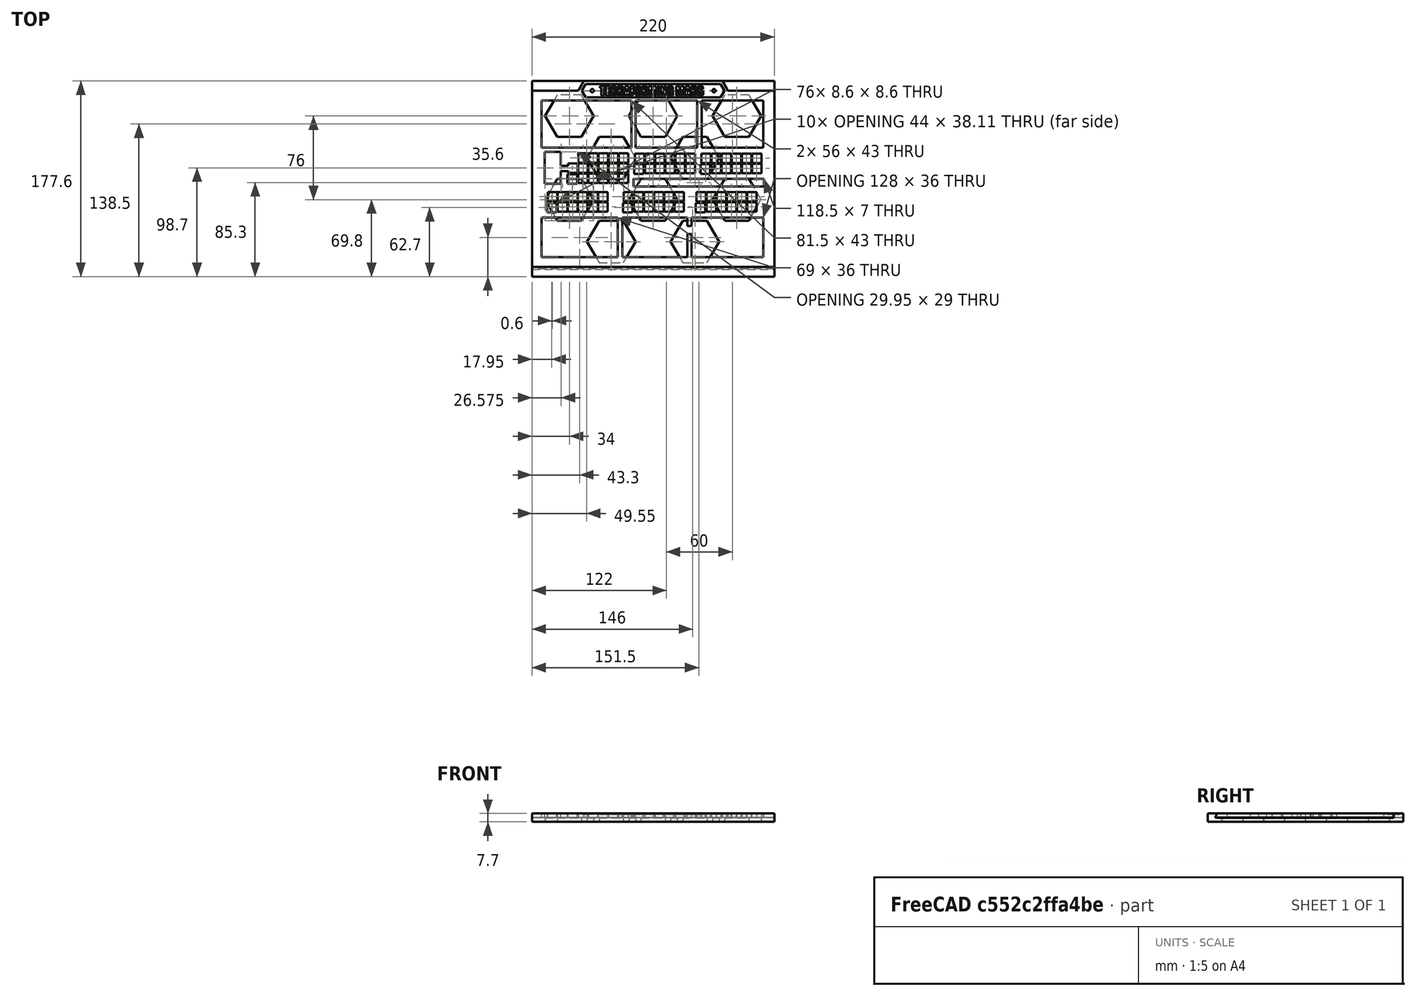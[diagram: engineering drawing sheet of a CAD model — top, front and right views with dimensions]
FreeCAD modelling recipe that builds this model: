
FCSTD DOCUMENT  (FreeCAD 0.21R33668 +26 (Git))
Label: overlay-full-v5
License: All rights reserved
LicenseURL: https://en.wikipedia.org/wiki/All_rights_reserved
objects: Sketcher::SketchObject×11, PartDesign::Pad×9, PartDesign::Pocket×5, Part::Feature×2, Part::Part2DObjectPython×2, PartDesign::Body×2, Mesh::Feature×1, Part::Refine×1, PartDesign::FeatureBase×1, Part::Extrusion×1
note: 48 computed .brp shape members not serialized (recipe doc carries the construction recipe); baked Part::Feature solids carry a one-line shape summary decoded from their .brp

FEATURE [Mesh::Feature] Terraforming_Mars_overlay
FEATURE [Part::Feature] Terraforming_Mars_overlay001
  shape: bbox 208 x 148 x 3.7 mm, 1736 faces, 0 solids (baked)
FEATURE [Part::Feature] Terraforming_Mars_overlay001_solid  label="Terraforming_Mars_overlay001 (Solid)"
  shape: bbox 208 x 148 x 3.7 mm, 1736 faces (baked)
FEATURE [Part::Refine] Terraforming_Mars_overlay001_solid001  label="Terraforming_Mars_overlay001 (Solid)001"
  Source = -> Terraforming_Mars_overlay001_solid
FEATURE [PartDesign::FeatureBase] BaseFeature
  BaseFeature = -> Terraforming_Mars_overlay001_solid001
FEATURE [Sketcher::SketchObject] Sketch
  ExternalGeometry = -> [BaseFeature]
  FullyConstrained = true
  MapMode = 5
  Placement = pos=(0,0,3.7) rot=(0,0,1;0rad)
  Support = -> [BaseFeature]
  sketch-geometry (8):
    g0: LineSegment StartX=6 StartY=154 StartZ=0 EndX=214 EndY=154 EndZ=0
    g1: LineSegment StartX=214 StartY=154 StartZ=0 EndX=214 EndY=6 EndZ=0
    g2: LineSegment StartX=214 StartY=6 StartZ=0 EndX=6 EndY=6 EndZ=0
    g3: LineSegment StartX=6 StartY=6 StartZ=0 EndX=6 EndY=154 EndZ=0
    g4: LineSegment StartX=0 StartY=160 StartZ=0 EndX=220 EndY=160 EndZ=0
    g5: LineSegment StartX=220 StartY=160 StartZ=0 EndX=220 EndY=0 EndZ=0
    g6: LineSegment StartX=220 StartY=0 StartZ=0 EndX=0 EndY=0 EndZ=0
    g7: LineSegment StartX=0 StartY=0 StartZ=0 EndX=0 EndY=160 EndZ=0
  constraints (22):
    c: Coincident(g0,g1)
    c: Coincident(g1,g2)
    c: Coincident(g2,g3)
    c: Coincident(g3,g0)
    c: Horizontal(g0)
    c: Horizontal(g2)
    c: Vertical(g1)
    c: Vertical(g3)
    c: Coincident(g0,g-3)
    c: Coincident(g1,g-4)
    c: Coincident(g4,g5)
    c: Coincident(g5,g6)
    c: Coincident(g6,g7)
    c: Coincident(g7,g4)
    c: Horizontal(g4)
    c: Horizontal(g6)
    c: Vertical(g5)
    c: Vertical(g7)
    c: DistanceX(g4,g0) = 6
    c: DistanceX(g0,g4) = 6
    c: DistanceY(g0,g4) = 6
    c: DistanceY(g5,g1) = 6
FEATURE [PartDesign::Pad] Pad
  BaseFeature = -> BaseFeature
  Direction = (0,0,1)
  Length = 10
  Length2 = 10
  Profile = -> Sketch
  ReferenceAxis = -> Sketch [N_Axis]
  Type = 3
  UpToFace = -> BaseFeature [Face1]
FEATURE [Sketcher::SketchObject] Sketch001
  ExternalGeometry = -> [Pad]
  FullyConstrained = true
  MapMode = 5
  Placement = pos=(0,0,3.7) rot=(0,0,1;0rad)
  Support = -> [Pad]
  sketch-geometry (5):
    g0: GeomPoint X=110 Y=160 Z=0
    g1: LineSegment StartX=42 StartY=160 StartZ=0 EndX=47.0807 EndY=168.8 EndZ=0
    g2: LineSegment StartX=47.0807 StartY=168.8 StartZ=0 EndX=172.919 EndY=168.8 EndZ=0
    g3: LineSegment StartX=172.919 StartY=168.8 StartZ=0 EndX=178 EndY=160 EndZ=0
    g4: LineSegment StartX=178 StartY=160 StartZ=0 EndX=42 EndY=160 EndZ=0
  constraints (13):
    c: Symmetric(g-3,g-3,g0)
    c: Coincident(g1,g2)
    c: Horizontal(g2)
    c: Coincident(g2,g3)
    c: Coincident(g3,g4)
    c: Coincident(g4,g1)
    c: Angle(g1,g4,g1) = 2.0944
    c: Angle(g4,g3,g3) = 2.0944
    c: DistanceY(g1,g1) = 8.8
    c: PointOnObject(g1,g-3)
    c: DistanceX(g-3,g1) = 42
    c: DistanceX(g3,g-3) = 42
    c: PointOnObject(g3,g-3)
FEATURE [PartDesign::Pad] Pad001
  BaseFeature = -> Pad
  Direction = (0,0,1)
  Length = 10
  Length2 = 10
  Profile = -> Sketch001
  ReferenceAxis = -> Sketch001 [N_Axis]
  Type = 3
  UpToFace = -> Pad [Face2]
FEATURE [Sketcher::SketchObject] Sketch002
  ExternalGeometry = -> [Pad001]
  FullyConstrained = true
  MapMode = 5
  Placement = pos=(0,0,3.7) rot=(0,0,1;0rad)
  Support = -> [Pad001]
  sketch-geometry (7):
    g0: GeomPoint X=110 Y=160 Z=0
    g1: LineSegment StartX=45.2332 StartY=160 StartZ=0 EndX=48.6973 EndY=166 EndZ=0
    g2: LineSegment StartX=48.6973 StartY=166 StartZ=0 EndX=171.303 EndY=166 EndZ=0
    g3: LineSegment StartX=171.303 StartY=166 StartZ=0 EndX=174.767 EndY=160 EndZ=0
    g4: LineSegment StartX=174.767 StartY=160 StartZ=0 EndX=171.303 EndY=154 EndZ=0
    g5: LineSegment StartX=171.303 StartY=154 StartZ=0 EndX=48.6973 EndY=154 EndZ=0
    g6: LineSegment StartX=48.6973 StartY=154 StartZ=0 EndX=45.2332 EndY=160 EndZ=0
  constraints (17):
    c: Symmetric(g-4,g-4,g0)
    c: PointOnObject(g1,g-4)
    c: Coincident(g1,g2)
    c: Horizontal(g2)
    c: Coincident(g2,g3)
    c: PointOnObject(g3,g-4)
    c: Coincident(g3,g4)
    c: PointOnObject(g4,g-5)
    c: Coincident(g4,g5)
    c: Coincident(g5,g6)
    c: Coincident(g6,g1)
    c: Parallel(g1,g-6)
    c: Symmetric(g5,g1,g-4)
    c: Symmetric(g4,g2,g-4)
    c: Parallel(g3,g-7)
    c: Distance(g1,g-6) = 2.8
    c: Distance(g2,g-7) = 2.8
FEATURE [PartDesign::Pocket] Pocket
  BaseFeature = -> Pad001
  Direction = (0,0,-1)
  Length = 1
  Length2 = 5
  Profile = -> Sketch002
  ReferenceAxis = -> Sketch002 [N_Axis]
  Type = 0
FEATURE [Part::Part2DObjectPython] ShapeString  # Draft 2D object (typed FeaturePython)
  FontFile = <path>
  MakeFace = true
  Placement = pos=(61.7,155.5,2.7) rot=(0,0,1;0rad)
  Size = 9
  String = TERRAFORMING MARS
  Tracking = 0
FEATURE [Sketcher::SketchObject] Sketch003
  ExternalGeometry = -> [Pocket]
  FullyConstrained = true
  MapMode = 5
  Placement = pos=(0,0,2.7) rot=(0,0,1;0rad)
  Support = -> [Pocket]
  sketch-geometry (3):
    g0: LineSegment StartX=45.2332 StartY=160 StartZ=0 EndX=174.767 EndY=160 EndZ=0
    g1: Circle CenterX=54.7332 CenterY=160 CenterZ=0 NormalX=0 NormalY=0 NormalZ=1 AngleXU=0 Radius=1.5
    g2: Circle CenterX=165.267 CenterY=160 CenterZ=0 NormalX=0 NormalY=0 NormalZ=1 AngleXU=0 Radius=1.5
  constraints (8):
    c: Coincident(g0,g-3)
    c: Coincident(g0,g-4)
    c: PointOnObject(g1,g0)
    c: PointOnObject(g2,g0)
    c: Diameter(g2) = 3
    c: Diameter(g1) = 3
    c: DistanceX(g0,g1) = 9.5
    c: DistanceX(g2,g0) = 9.5
FEATURE [PartDesign::Pad] Pad002
  BaseFeature = -> Pocket
  Direction = (0,0,1)
  Length = 1
  Length2 = 10
  Profile = -> Sketch003
  ReferenceAxis = -> Sketch003 [N_Axis]
  Type = 0
FEATURE [PartDesign::Pad] Pad003
  BaseFeature = -> Pad002
  Direction = (0,-1,0)
  Length = 2
  Length2 = 10
  Profile = -> Pad002 [Face352]
  Type = 0
FEATURE [Sketcher::SketchObject] Sketch004
  ExternalGeometry = -> [Pad003]
  FullyConstrained = true
  MapMode = 5
  Placement = pos=(220,0,0) rot=(0.57735,0.57735,0.57735;2.0944rad)
  Support = -> [Pad003]
  sketch-geometry (3):
    g0: LineSegment StartX=0 StartY=3.7 StartZ=0 EndX=-2 EndY=0 EndZ=0
    g1: LineSegment StartX=-2 StartY=0 StartZ=0 EndX=-2 EndY=3.7 EndZ=0
    g2: LineSegment StartX=-2 StartY=3.7 StartZ=0 EndX=0 EndY=3.7 EndZ=0
  constraints (6):
    c: Coincident(g-4,g0)
    c: Coincident(g0,g-3)
    c: Coincident(g0,g1)
    c: Coincident(g1,g-4)
    c: Coincident(g1,g2)
    c: Coincident(g2,g0)
FEATURE [PartDesign::Pocket] Pocket001
  BaseFeature = -> Pad003
  Direction = (-1,0,0)
  Length = 5
  Length2 = 5
  Profile = -> Sketch004
  ReferenceAxis = -> Sketch004 [N_Axis]
  Type = 1
FEATURE [PartDesign::Body] Body  label="Front"
  BaseFeature = -> Terraforming_Mars_overlay001_solid001
  Group = -> [BaseFeature,Sketch,Pad,Sketch001,Pad001,Sketch002,Pocket,Sketch003,Pad002,Pad003,Sketch004,Pocket001]
  Origin = -> Origin
  Tip = -> Pocket001
FEATURE [Part::Extrusion] Extrude  label="Text"
  Base = -> ShapeString
  Dir = (0,0,1)
  DirMode = 2
  FaceMakerClass = Part::FaceMakerBullseye
  LengthFwd = 1
  LengthRev = 0
  Solid = false
  Symmetric = false
FEATURE [Sketcher::SketchObject] Sketch005
  FullyConstrained = true
  MapMode = 5
  Support = -> [XY_Plane001]
  sketch-geometry (4):
    g0: LineSegment StartX=0 StartY=160 StartZ=0 EndX=220 EndY=160 EndZ=0
    g1: LineSegment StartX=220 StartY=160 StartZ=0 EndX=220 EndY=0 EndZ=0
    g2: LineSegment StartX=220 StartY=0 StartZ=0 EndX=0 EndY=0 EndZ=0
    g3: LineSegment StartX=0 StartY=0 StartZ=0 EndX=0 EndY=160 EndZ=0
  constraints (12):
    c: Coincident(g0,g1)
    c: Coincident(g1,g2)
    c: Coincident(g2,g3)
    c: Coincident(g3,g0)
    c: Horizontal(g0)
    c: Horizontal(g2)
    c: Vertical(g1)
    c: Vertical(g3)
    c: PointOnObject(g1,g-1)
    c: PointOnObject(g0,g-2)
    c: DistanceX(g0,g0) = 220
    c: DistanceY(g1,g1) = 160
FEATURE [PartDesign::Pad] Pad004
  Direction = (0,0,1)
  Length = 4
  Length2 = 10
  Profile = -> Sketch005
  ReferenceAxis = -> Sketch005 [N_Axis]
  Reversed = true
  Type = 0
FEATURE [PartDesign::Pad] Pad005
  BaseFeature = -> Pad004
  Direction = (0,-1,0)
  Length = 8.8
  Length2 = 10
  Profile = -> Pad004 [Face3]
  Type = 0
FEATURE [PartDesign::Pad] Pad006
  BaseFeature = -> Pad005
  Direction = (0,0,1)
  Length = 3.7
  Length2 = 10
  Profile = -> Pad005 [Face8]
  Type = 0
FEATURE [Sketcher::SketchObject] Sketch006
  ExternalGeometry = -> [Pad006]
  FullyConstrained = true
  MapMode = 5
  Placement = pos=(0,0,0) rot=(0.57735,-0.57735,-0.57735;2.0944rad)
  Support = -> [Pad006]
  sketch-geometry (4):
    g0: LineSegment StartX=0 StartY=0 StartZ=0 EndX=2.1 EndY=0 EndZ=0
    g1: LineSegment StartX=0.1 StartY=3.7 StartZ=0 EndX=2.1 EndY=0 EndZ=0
    g2: LineSegment StartX=0 StartY=3.7 StartZ=0 EndX=0 EndY=0 EndZ=0
    g3: LineSegment StartX=0.1 StartY=3.7 StartZ=0 EndX=0 EndY=3.7 EndZ=0
  constraints (10):
    c: Coincident(g-1,g0)
    c: PointOnObject(g0,g-1)
    c: Coincident(g1,g0)
    c: DistanceX(g0,g0) = 2.1
    c: PointOnObject(g1,g-3)
    c: Coincident(g2,g-3)
    c: Coincident(g2,g0)
    c: Coincident(g3,g1)
    c: Coincident(g3,g2)
    c: DistanceX(g3,g3) = 0.1
FEATURE [PartDesign::Pocket] Pocket002
  BaseFeature = -> Pad006
  Direction = (1,0,0)
  Length = 5
  Length2 = 5
  Profile = -> Sketch006
  ReferenceAxis = -> Sketch006 [N_Axis]
  Type = 1
FEATURE [PartDesign::Pad] Pad007
  BaseFeature = -> Pocket002
  Direction = (0,1,0)
  Length = 8.8
  Length2 = 10
  Profile = -> Pocket002 [Face1]
  Type = 0
FEATURE [Sketcher::SketchObject] Sketch007
  ExternalGeometry = -> [Pad007]
  FullyConstrained = true
  MapMode = 5
  Placement = pos=(0,0,0) rot=(0.57735,-0.57735,-0.57735;2.0944rad)
  Support = -> [Pad007]
  sketch-geometry (3):
    g0: LineSegment StartX=4.63784 StartY=3.7 StartZ=0 EndX=8.8 EndY=-4 EndZ=0
    g1: LineSegment StartX=8.8 StartY=-4 StartZ=0 EndX=8.8 EndY=3.7 EndZ=0
    g2: LineSegment StartX=8.8 StartY=3.7 StartZ=0 EndX=4.63784 EndY=3.7 EndZ=0
  constraints (7):
    c: PointOnObject(g0,g-3)
    c: Coincident(g0,g-6)
    c: Coincident(g1,g0)
    c: Coincident(g1,g-5)
    c: Coincident(g2,g1)
    c: Coincident(g2,g0)
    c: Parallel(g0,g-4)
FEATURE [Sketcher::SketchObject] Sketch008
  ExternalGeometry = -> [Pad007]
  FullyConstrained = true
  MapMode = 5
  Support = -> [Pad007]
  sketch-geometry (12):
    g0: LineSegment StartX=0 StartY=160 StartZ=0 EndX=42 EndY=160 EndZ=0
    g1: LineSegment StartX=42 StartY=160 StartZ=0 EndX=47.0807 EndY=168.8 EndZ=0
    g2: LineSegment StartX=0 StartY=168.8 StartZ=0 EndX=46.9652 EndY=168.8 EndZ=0
    g3: LineSegment StartX=46.9652 StartY=168.8 StartZ=0 EndX=41.9423 EndY=160.1 EndZ=0
    g4: LineSegment StartX=41.9423 StartY=160.1 StartZ=0 EndX=0 EndY=160.1 EndZ=0
    g5: LineSegment StartX=0 StartY=160.1 StartZ=0 EndX=0 EndY=168.8 EndZ=0
    g6: LineSegment StartX=172.919 StartY=168.8 StartZ=0 EndX=178 EndY=160 EndZ=0
    g7: LineSegment StartX=178 StartY=160 StartZ=0 EndX=220 EndY=160 EndZ=0
    g8: LineSegment StartX=173.035 StartY=168.8 StartZ=0 EndX=220 EndY=168.8 EndZ=0
    g9: LineSegment StartX=220 StartY=168.8 StartZ=0 EndX=220 EndY=160.1 EndZ=0
    g10: LineSegment StartX=220 StartY=160.1 StartZ=0 EndX=178.058 EndY=160.1 EndZ=0
    g11: LineSegment StartX=178.058 StartY=160.1 StartZ=0 EndX=173.035 EndY=168.8 EndZ=0
  constraints (34):
    c: Coincident(g-4,g0)
    c: PointOnObject(g0,g-4)
    c: Coincident(g0,g1)
    c: PointOnObject(g1,g-3)
    c: DistanceX(g0,g0) = 42
    c: Angle(g-4,g1,g0) = 1.0472
    c: Coincident(g-3,g2)
    c: PointOnObject(g2,g-3)
    c: Coincident(g2,g3)
    c: Coincident(g3,g4)
    c: PointOnObject(g4,g-2)
    c: Horizontal(g4)
    c: Coincident(g4,g5)
    c: Coincident(g5,g2)
    c: Parallel(g3,g1)
    c: Distance(g4,g0) = 0.1
    c: Distance(g2,g1) = 0.1
    c: PointOnObject(g6,g-3)
    c: PointOnObject(g6,g-4)
    c: Coincident(g7,g6)
    c: Coincident(g7,g-5)
    c: DistanceX(g7,g7) = 42
    c: Angle(g6,g-4,g6) = 1.0472
    c: PointOnObject(g8,g-3)
    c: Coincident(g8,g-5)
    c: Coincident(g8,g9)
    c: PointOnObject(g9,g-5)
    c: Coincident(g9,g10)
    c: Horizontal(g10)
    c: Coincident(g10,g11)
    c: Coincident(g11,g8)
    c: Distance(g8,g6) = 0.1
    c: Parallel(g11,g6)
    c: Distance(g9,g7) = 0.1
FEATURE [PartDesign::Pad] Pad008
  BaseFeature = -> Pad007
  Direction = (0,0,1)
  Length = 3.7
  Length2 = 10
  Profile = -> Sketch008
  ReferenceAxis = -> Sketch008 [N_Axis]
  Type = 0
FEATURE [Sketcher::SketchObject] Sketch009
  ExternalGeometry = -> [Pad008]
  FullyConstrained = true
  MapMode = 5
  Support = -> [Pad008]
  sketch-geometry (4):
    g0: LineSegment StartX=0 StartY=0 StartZ=0 EndX=220 EndY=0 EndZ=0
    g1: LineSegment StartX=220 StartY=0 StartZ=0 EndX=220 EndY=160 EndZ=0
    g2: LineSegment StartX=220 StartY=160 StartZ=0 EndX=0 EndY=160 EndZ=0
    g3: LineSegment StartX=0 StartY=160 StartZ=0 EndX=0 EndY=0 EndZ=0
  constraints (10):
    c: Coincident(g0,g1)
    c: Coincident(g1,g2)
    c: Coincident(g2,g3)
    c: Coincident(g3,g0)
    c: Horizontal(g0)
    c: Horizontal(g2)
    c: Vertical(g1)
    c: Vertical(g3)
    c: Coincident(g0,g-5)
    c: Coincident(g1,g-4)
FEATURE [PartDesign::Pocket] Pocket003
  BaseFeature = -> Pad008
  Direction = (0,0,-1)
  Length = 0.3
  Length2 = 5
  Profile = -> Sketch009
  ReferenceAxis = -> Sketch009 [N_Axis]
  Type = 0
FEATURE [Part::Part2DObjectPython] ShapeString001  # Draft 2D object (typed FeaturePython)
  FontFile = <path>
  MakeFace = true
  Placement = pos=(12.35,20,0) rot=(0,0,1;1e-06rad)
  Size = 120
  String = T M
  Tracking = 0
FEATURE [Sketcher::SketchObject] Sketch010
  ExternalGeometry = -> [Pocket003]
  FullyConstrained = true
  MapMode = 5
  Placement = pos=(0,0,-0.3) rot=(0,0,1;0rad)
  Support = -> [Pocket003]
  sketch-geometry (79):
    g0: LineSegment StartX=220 StartY=137 StartZ=0 EndX=0 EndY=137 EndZ=0
    g1: LineSegment StartX=220 StartY=99 StartZ=0 EndX=0 EndY=99 EndZ=0
    g2: LineSegment StartX=220 StartY=61 StartZ=0 EndX=0 EndY=61 EndZ=0
    g3: LineSegment StartX=0 StartY=23 StartZ=0 EndX=220 EndY=23 EndZ=0
    g4: LineSegment StartX=94 StartY=99 StartZ=0 EndX=83 EndY=118.053 EndZ=0
    g5: LineSegment StartX=83 StartY=118.053 StartZ=0 EndX=61 EndY=118.053 EndZ=0
    g6: LineSegment StartX=61 StartY=118.053 StartZ=0 EndX=50 EndY=99 EndZ=0
    g7: LineSegment StartX=50 StartY=99 StartZ=0 EndX=61 EndY=79.9474 EndZ=0
    g8: LineSegment StartX=61 StartY=79.9474 StartZ=0 EndX=83 EndY=79.9474 EndZ=0
    g9: LineSegment StartX=83 StartY=79.9474 StartZ=0 EndX=94 EndY=99 EndZ=0
    g10: Circle CenterX=72 CenterY=99 CenterZ=0 NormalX=0 NormalY=0 NormalZ=1 AngleXU=0 Radius=22
    g11: LineSegment StartX=56 StartY=137 StartZ=0 EndX=45 EndY=156.053 EndZ=0
    g12: LineSegment StartX=45 StartY=156.053 StartZ=0 EndX=23 EndY=156.053 EndZ=0
    g13: LineSegment StartX=23 StartY=156.053 StartZ=0 EndX=12 EndY=137 EndZ=0
    g14: LineSegment StartX=12 StartY=137 StartZ=0 EndX=23 EndY=117.947 EndZ=0
    g15: LineSegment StartX=23 StartY=117.947 StartZ=0 EndX=45 EndY=117.947 EndZ=0
    g16: LineSegment StartX=45 StartY=117.947 StartZ=0 EndX=56 EndY=137 EndZ=0
    g17: Circle CenterX=34 CenterY=137 CenterZ=0 NormalX=0 NormalY=0 NormalZ=1 AngleXU=0 Radius=22
    g18: LineSegment StartX=132 StartY=137 StartZ=0 EndX=121 EndY=156.053 EndZ=0
    g19: LineSegment StartX=121 StartY=156.053 StartZ=0 EndX=99 EndY=156.053 EndZ=0
    g20: LineSegment StartX=99 StartY=156.053 StartZ=0 EndX=88 EndY=137 EndZ=0
    g21: LineSegment StartX=88 StartY=137 StartZ=0 EndX=99 EndY=117.947 EndZ=0
    g22: LineSegment StartX=99 StartY=117.947 StartZ=0 EndX=121 EndY=117.947 EndZ=0
    g23: LineSegment StartX=121 StartY=117.947 StartZ=0 EndX=132 EndY=137 EndZ=0
    g24: Circle CenterX=110 CenterY=137 CenterZ=0 NormalX=0 NormalY=0 NormalZ=1 AngleXU=0 Radius=22
    g25: LineSegment StartX=170 StartY=99 StartZ=0 EndX=159 EndY=118.053 EndZ=0
    g26: LineSegment StartX=159 StartY=118.053 StartZ=0 EndX=137 EndY=118.053 EndZ=0
    g27: LineSegment StartX=137 StartY=118.053 StartZ=0 EndX=126 EndY=99 EndZ=0
    g28: LineSegment StartX=126 StartY=99 StartZ=0 EndX=137 EndY=79.9474 EndZ=0
    g29: LineSegment StartX=137 StartY=79.9474 StartZ=0 EndX=159 EndY=79.9474 EndZ=0
    g30: LineSegment StartX=159 StartY=79.9474 StartZ=0 EndX=170 EndY=99 EndZ=0
    g31: Circle CenterX=148 CenterY=99 CenterZ=0 NormalX=0 NormalY=0 NormalZ=1 AngleXU=0 Radius=22
    g32: LineSegment StartX=208 StartY=137 StartZ=0 EndX=197 EndY=156.053 EndZ=0
    g33: LineSegment StartX=197 StartY=156.053 StartZ=0 EndX=175 EndY=156.053 EndZ=0
    g34: LineSegment StartX=175 StartY=156.053 StartZ=0 EndX=164 EndY=137 EndZ=0
    g35: LineSegment StartX=164 StartY=137 StartZ=0 EndX=175 EndY=117.947 EndZ=0
    g36: LineSegment StartX=175 StartY=117.947 StartZ=0 EndX=197 EndY=117.947 EndZ=0
    g37: LineSegment StartX=197 StartY=117.947 StartZ=0 EndX=208 EndY=137 EndZ=0
    g38: Circle CenterX=186 CenterY=137 CenterZ=0 NormalX=0 NormalY=0 NormalZ=1 AngleXU=0 Radius=22
    g39: LineSegment StartX=34 StartY=160 StartZ=0 EndX=34 EndY=0 EndZ=0
    g40: LineSegment StartX=72 StartY=160 StartZ=0 EndX=72 EndY=0 EndZ=0
    g41: LineSegment StartX=110 StartY=160 StartZ=0 EndX=110 EndY=0 EndZ=0
    g42: LineSegment StartX=148 StartY=160 StartZ=0 EndX=148 EndY=0 EndZ=0
    g43: LineSegment StartX=186 StartY=160 StartZ=0 EndX=186 EndY=0 EndZ=0
    g44: LineSegment StartX=208 StartY=61 StartZ=0 EndX=197 EndY=80.0526 EndZ=0
    g45: LineSegment StartX=197 StartY=80.0526 StartZ=0 EndX=175 EndY=80.0526 EndZ=0
    g46: LineSegment StartX=175 StartY=80.0526 StartZ=0 EndX=164 EndY=61 EndZ=0
    g47: LineSegment StartX=164 StartY=61 StartZ=0 EndX=175 EndY=41.9474 EndZ=0
    g48: LineSegment StartX=175 StartY=41.9474 StartZ=0 EndX=197 EndY=41.9474 EndZ=0
    g49: LineSegment StartX=197 StartY=41.9474 StartZ=0 EndX=208 EndY=61 EndZ=0
    g50: Circle CenterX=186 CenterY=61 CenterZ=0 NormalX=0 NormalY=0 NormalZ=1 AngleXU=0 Radius=22
    g51: LineSegment StartX=132 StartY=61 StartZ=0 EndX=121 EndY=80.0526 EndZ=0
    g52: LineSegment StartX=121 StartY=80.0526 StartZ=0 EndX=99 EndY=80.0526 EndZ=0
    g53: LineSegment StartX=99 StartY=80.0526 StartZ=0 EndX=88 EndY=61 EndZ=0
    g54: LineSegment StartX=88 StartY=61 StartZ=0 EndX=99 EndY=41.9474 EndZ=0
    g55: LineSegment StartX=99 StartY=41.9474 StartZ=0 EndX=121 EndY=41.9474 EndZ=0
    g56: LineSegment StartX=121 StartY=41.9474 StartZ=0 EndX=132 EndY=61 EndZ=0
    g57: Circle CenterX=110 CenterY=61 CenterZ=0 NormalX=0 NormalY=0 NormalZ=1 AngleXU=0 Radius=22
    g58: LineSegment StartX=56 StartY=61 StartZ=0 EndX=45 EndY=80.0526 EndZ=0
    g59: LineSegment StartX=45 StartY=80.0526 StartZ=0 EndX=23 EndY=80.0526 EndZ=0
    g60: LineSegment StartX=23 StartY=80.0526 StartZ=0 EndX=12 EndY=61 EndZ=0
    g61: LineSegment StartX=12 StartY=61 StartZ=0 EndX=23 EndY=41.9474 EndZ=0
    g62: LineSegment StartX=23 StartY=41.9474 StartZ=0 EndX=45 EndY=41.9474 EndZ=0
    g63: LineSegment StartX=45 StartY=41.9474 StartZ=0 EndX=56 EndY=61 EndZ=0
    g64: Circle CenterX=34 CenterY=61 CenterZ=0 NormalX=0 NormalY=0 NormalZ=1 AngleXU=0 Radius=22
    g65: LineSegment StartX=94 StartY=23 StartZ=0 EndX=83 EndY=42.0526 EndZ=0
    g66: LineSegment StartX=83 StartY=42.0526 StartZ=0 EndX=61 EndY=42.0526 EndZ=0
    g67: LineSegment StartX=61 StartY=42.0526 StartZ=0 EndX=50 EndY=23 EndZ=0
    g68: LineSegment StartX=50 StartY=23 StartZ=0 EndX=61 EndY=3.94744 EndZ=0
    g69: LineSegment StartX=61 StartY=3.94744 StartZ=0 EndX=83 EndY=3.94744 EndZ=0
    g70: LineSegment StartX=83 StartY=3.94744 StartZ=0 EndX=94 EndY=23 EndZ=0
    g71: Circle CenterX=72 CenterY=23 CenterZ=0 NormalX=0 NormalY=0 NormalZ=1 AngleXU=0 Radius=22
    g72: LineSegment StartX=170 StartY=23 StartZ=0 EndX=159 EndY=42.0526 EndZ=0
    g73: LineSegment StartX=159 StartY=42.0526 StartZ=0 EndX=137 EndY=42.0526 EndZ=0
    g74: LineSegment StartX=137 StartY=42.0526 StartZ=0 EndX=126 EndY=23 EndZ=0
    g75: LineSegment StartX=126 StartY=23 StartZ=0 EndX=137 EndY=3.94744 EndZ=0
    g76: LineSegment StartX=137 StartY=3.94744 StartZ=0 EndX=159 EndY=3.94744 EndZ=0
    g77: LineSegment StartX=159 StartY=3.94744 StartZ=0 EndX=170 EndY=23 EndZ=0
    g78: Circle CenterX=148 CenterY=23 CenterZ=0 NormalX=0 NormalY=0 NormalZ=1 AngleXU=0 Radius=22
  constraints (206):
    c: PointOnObject(g0,g-5)
    c: Horizontal(g0)
    c: PointOnObject(g1,g-5)
    c: PointOnObject(g1,g-3)
    c: Horizontal(g1)
    c: PointOnObject(g2,g-5)
    c: PointOnObject(g2,g-2)
    c: Horizontal(g2)
    c: PointOnObject(g0,g-3)
    c: DistanceY(g0,g-4) = 23
    c: DistanceY(g1,g0) = 38
    c: DistanceY(g2,g1) = 38
    c: PointOnObject(g3,g-3)
    c: PointOnObject(g3,g-5)
    c: Horizontal(g3)
    c: DistanceY(g3,g2) = 38
    c: Coincident(g4,g5)
    c: Coincident(g5,g6)
    c: Coincident(g6,g7)
    c: Coincident(g7,g8)
    c: Coincident(g8,g9)
    c: Coincident(g9,g4)
    c: Equal(g4, g5-g9) x5
    c: PointOnObject(g4,g10)
    c: PointOnObject(g5,g10)
    c: PointOnObject(g6,g10)
    c: PointOnObject(g7,g10)
    c: PointOnObject(g8,g10)
    c: PointOnObject(g9,g10)
    c: PointOnObject(g10,g1)
    c: PointOnObject(g9,g1)
    c: Coincident(g11,g12)
    c: Coincident(g12,g13)
    c: Coincident(g13,g14)
    c: Coincident(g14,g15)
    c: Coincident(g15,g16)
    c: Coincident(g16,g11)
    c: Equal(g11, g12-g16) x5
    c: PointOnObject(g11,g17)
    c: PointOnObject(g12,g17)
    c: PointOnObject(g13,g17)
    c: PointOnObject(g14,g17)
    c: PointOnObject(g15,g17)
    c: PointOnObject(g16,g17)
    c: PointOnObject(g17,g0)
    c: PointOnObject(g16,g0)
    c: Coincident(g18,g19)
    c: Coincident(g19,g20)
    c: Coincident(g20,g21)
    c: Coincident(g21,g22)
    c: Coincident(g22,g23)
    c: Coincident(g23,g18)
    c: Equal(g18, g19-g23) x5
    c: PointOnObject(g18,g24)
    c: PointOnObject(g19,g24)
    c: PointOnObject(g20,g24)
    c: PointOnObject(g21,g24)
    c: PointOnObject(g22,g24)
    c: PointOnObject(g23,g24)
    c: PointOnObject(g24,g0)
    c: PointOnObject(g23,g0)
    c: Coincident(g25,g26)
    c: Coincident(g26,g27)
    c: Coincident(g27,g28)
    c: Coincident(g28,g29)
    c: Coincident(g29,g30)
    c: Coincident(g30,g25)
    c: Equal(g25, g26-g30) x5
    c: PointOnObject(g25,g31)
    c: PointOnObject(g26,g31)
    c: PointOnObject(g27,g31)
    c: PointOnObject(g28,g31)
    c: PointOnObject(g29,g31)
    c: PointOnObject(g30,g31)
    c: PointOnObject(g31,g1)
    c: PointOnObject(g30,g1)
    c: Coincident(g32,g33)
    c: Coincident(g33,g34)
    c: Coincident(g34,g35)
    c: Coincident(g35,g36)
    c: Coincident(g36,g37)
    c: Coincident(g37,g32)
    c: Equal(g32, g33-g37) x5
    c: PointOnObject(g32,g38)
    c: PointOnObject(g33,g38)
    c: PointOnObject(g34,g38)
    c: PointOnObject(g35,g38)
    c: PointOnObject(g36,g38)
    c: PointOnObject(g37,g38)
    c: PointOnObject(g38,g0)
    c: PointOnObject(g37,g0)
    c: PointOnObject(g39,g-4)
    c: PointOnObject(g39,g-6)
    c: Vertical(g39)
    c: PointOnObject(g40,g-4)
    c: PointOnObject(g40,g-6)
    c: Vertical(g40)
    c: PointOnObject(g41,g-4)
    c: PointOnObject(g41,g-6)
    c: Vertical(g41)
    c: PointOnObject(g42,g-4)
    c: PointOnObject(g42,g-6)
    c: Vertical(g42)
    c: PointOnObject(g43,g-4)
    c: PointOnObject(g43,g-6)
    c: Vertical(g43)
    c: DistanceX(g39,g40) = 38
    c: DistanceX(g40,g41) = 38
    c: DistanceX(g41,g42) = 38
    c: DistanceX(g42,g43) = 38
    c: DistanceX(g-4,g39) = 34
    c: PointOnObject(g17,g39)
    c: Radius(g17) = 22
    c: PointOnObject(g10,g40)
    c: Radius(g10) = 22
    c: Radius(g24) = 22
    c: Radius(g31) = 22
    c: Radius(g38) = 22
    c: PointOnObject(g31,g42)
    c: PointOnObject(g38,g43)
    c: Coincident(g44,g45)
    c: Coincident(g45,g46)
    c: Coincident(g46,g47)
    c: Coincident(g47,g48)
    c: Coincident(g48,g49)
    c: Coincident(g49,g44)
    c: Equal(g44, g45-g49) x5
    c: PointOnObject(g44,g50)
    c: PointOnObject(g45,g50)
    c: PointOnObject(g46,g50)
    c: PointOnObject(g47,g50)
    c: PointOnObject(g48,g50)
    c: PointOnObject(g49,g50)
    c: PointOnObject(g50,g2)
    c: PointOnObject(g49,g2)
    c: Coincident(g51,g52)
    c: Coincident(g52,g53)
    c: Coincident(g53,g54)
    c: Coincident(g54,g55)
    c: Coincident(g55,g56)
    c: Coincident(g56,g51)
    c: Equal(g51, g52-g56) x5
    c: PointOnObject(g51,g57)
    c: PointOnObject(g52,g57)
    c: PointOnObject(g53,g57)
    c: PointOnObject(g54,g57)
    c: PointOnObject(g55,g57)
    c: PointOnObject(g56,g57)
    c: PointOnObject(g57,g2)
    c: PointOnObject(g56,g2)
    c: Coincident(g58,g59)
    c: Coincident(g59,g60)
    c: Coincident(g60,g61)
    c: Coincident(g61,g62)
    c: Coincident(g62,g63)
    c: Coincident(g63,g58)
    c: Equal(g58, g59-g63) x5
    c: PointOnObject(g58,g64)
    c: PointOnObject(g59,g64)
    c: PointOnObject(g60,g64)
    c: PointOnObject(g61,g64)
    c: PointOnObject(g62,g64)
    c: PointOnObject(g63,g64)
    c: PointOnObject(g64,g2)
    c: PointOnObject(g63,g2)
    c: Coincident(g65,g66)
    c: Coincident(g66,g67)
    c: Coincident(g67,g68)
    c: Coincident(g68,g69)
    c: Coincident(g69,g70)
    c: Coincident(g70,g65)
    c: Equal(g65, g66-g70) x5
    c: PointOnObject(g65,g71)
    c: PointOnObject(g66,g71)
    c: PointOnObject(g67,g71)
    c: PointOnObject(g68,g71)
    c: PointOnObject(g69,g71)
    c: PointOnObject(g70,g71)
    c: PointOnObject(g71,g3)
    c: PointOnObject(g70,g3)
    c: Coincident(g72,g73)
    c: Coincident(g73,g74)
    c: Coincident(g74,g75)
    c: Coincident(g75,g76)
    c: Coincident(g76,g77)
    c: Coincident(g77,g72)
    c: Equal(g72, g73-g77) x5
    c: PointOnObject(g72,g78)
    c: PointOnObject(g73,g78)
    c: PointOnObject(g74,g78)
    c: PointOnObject(g75,g78)
    c: PointOnObject(g76,g78)
    c: PointOnObject(g77,g78)
    c: PointOnObject(g78,g3)
    c: PointOnObject(g77,g3)
    c: PointOnObject(g50,g43)
    c: PointOnObject(g57,g41)
    c: PointOnObject(g64,g39)
    c: PointOnObject(g71,g40)
    c: PointOnObject(g78,g42)
    c: Radius(g64) = 22
    c: Radius(g57) = 22
    c: Radius(g50) = 22
    c: Radius(g78) = 22
    c: Radius(g71) = 22
    c: PointOnObject(g24,g41)
FEATURE [PartDesign::Pocket] Pocket004
  BaseFeature = -> Pocket003
  Direction = (0,0,-1)
  Length = 5
  Length2 = 5
  Profile = -> Sketch010
  ReferenceAxis = -> Sketch010 [N_Axis]
  Type = 1
FEATURE [PartDesign::Body] Body001  label="Back"
  Group = -> [Sketch005,Pad004,Pad005,Pad006,Sketch006,Pocket002,Pad007,Sketch007,Sketch008,Pad008,Sketch009,Pocket003,Sketch010,Pocket004]
  Origin = -> Origin001
  Tip = -> Pocket004
note: 2 file-system paths scrubbed to <path> (originals preserved in the JSON sidecar)
